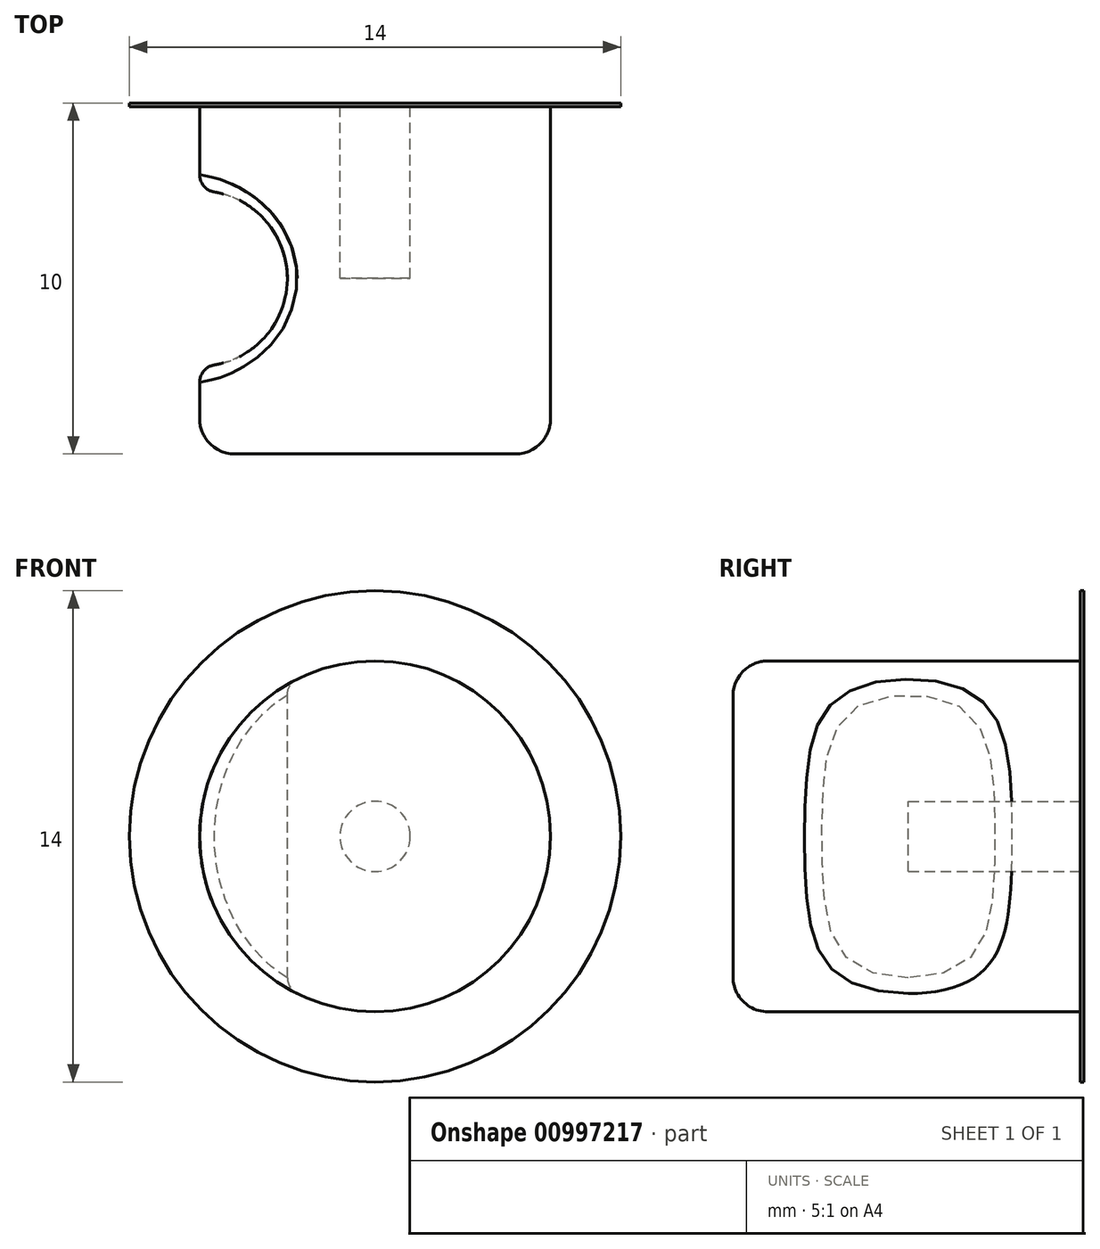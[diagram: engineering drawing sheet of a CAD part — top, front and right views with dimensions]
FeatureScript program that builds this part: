
annotation { "Feature Type Name" : "Feature", "Feature Type Description" : "" }
export const myFeature = defineFeature(function(context is Context, id is Id, definition is map)
    precondition{}
    {
        {
            var Q0;
            Q0=qCreatedBy(makeId("Front.planeOp"),FACE);
            var sketch = newSketch(context, id + "F0", { "sketchPlane" : qUnion([Q0])});
            skCircle(sketch, "E0", {"center": v(0, 0) * mm, "radius": 7 * mm});
            skCircle(sketch, "E1", {"center": v(0, 0) * mm, "radius": 5 * mm});
            skSolve(sketch);
        }
        {
            var Q0;
            Q0=makeQuery(id+"F0.imprint","IMPRINT",FACE,{"disambiguationData":[TD([[makeQuery(id+"F0.imprint","IMPRINT",EDGE,{"derivedFrom":sQuery(id+"F0.wireOp",EDGE,"E1")}),1.0]])]});
            extrude(context, id + "F1", {"entities" : qUnion([Q0]), "depth" : 10 * mm, "offsetDistance" : 25 * mm});
        }
        {
            var Q0;
            Q0=qCreatedBy(makeId("Top.planeOp"),FACE);
            var sketch = newSketch(context, id + "F2", { "sketchPlane" : qUnion([Q0])});
            skCircle(sketch, "E2", {"center": v(-5, -5) * mm, "radius": 2.5 * mm});
            skLineSegment(sketch, "E3", {"start": v(-5, 0.87) * mm, "end": v(-5, -10.87) * mm, "construction": true});
            skSolve(sketch);
        }
        {
            var Q0;
            Q0=makeQuery(id+"F2.imprint","IMPRINT",FACE,{"disambiguationData":[TD([[makeQuery(id+"F2.imprint","IMPRINT",EDGE,{"derivedFrom":sQuery(id+"F2.wireOp",EDGE,"E2")}),1.0]])]});
            extrude(context, id + "F3", {"entities" : qUnion([Q0]), "operationType" : NewBodyOperationType.REMOVE, "endBound" : BoundingType.SYMMETRIC, "oppositeDirection" : true, "depth" : 25 * mm, "offsetDistance" : 25 * mm});
        }
        {
            var Q0;
            Q0 = qSketchRegion(id + "F0", true);
            extrude(context, id + "F4", {"entities" : qUnion([Q0]), "operationType" : NewBodyOperationType.ADD, "depth" : 0.1 * mm, "offsetDistance" : 25 * mm});
        }
        {
            var Q0;
            Q0=makeQuery(id+"F4.opExtrude","CAP_EDGE",EDGE,{"disambiguationData":[OSD([sQuery(id+"F0.wireOp",EDGE,"E1")])],"isStart":false});
            var Q1;
            Q1=makeQuery(id+"F1.opExtrude","CAP_EDGE",EDGE,{"disambiguationData":[OSD([sQuery(id+"F0.wireOp",EDGE,"E1")])],"isStart":false});
            fillet(context, id + "F5", {"entities" : qUnion([Q0, Q1]), "radius" : 1 * mm, "tangentPropagation" : true, "allowEdgeOverflow" : false});
        }
        {
            var Q0;
            Q0=makeQuery(id+"F3.boolean.opBoolean","INTERSECT",EDGE,{"derivedFrom":[makeQuery(id+"F1.opExtrude","SWEPT_FACE",FACE,{"disambiguationData":[OSD([sQuery(id+"F0.wireOp",EDGE,"E1")])]}),makeQuery(id+"F3.opExtrude","SWEPT_FACE",FACE,{"disambiguationData":[OSD([sQuery(id+"F2.wireOp",EDGE,"E2")])]})]});
            fillet(context, id + "F6", {"entities" : qUnion([Q0]), "radius" : 0.5 * mm, "tangentPropagation" : true, "allowEdgeOverflow" : false});
        }
        {
            var Q0;
            Q0=qCreatedBy(makeId("Front.planeOp"),FACE);
            var sketch = newSketch(context, id + "F7", { "sketchPlane" : qUnion([Q0])});
            skCircle(sketch, "E4", {"center": v(0, 0) * mm, "radius": 1 * mm});
            skSolve(sketch);
        }
        {
            var Q0;
            Q0 = qSketchRegion(id + "F7", true);
            extrude(context, id + "F8", {"entities" : qUnion([Q0]), "operationType" : NewBodyOperationType.REMOVE, "depth" : 5 * mm, "offsetDistance" : 25 * mm});
        }
    });
